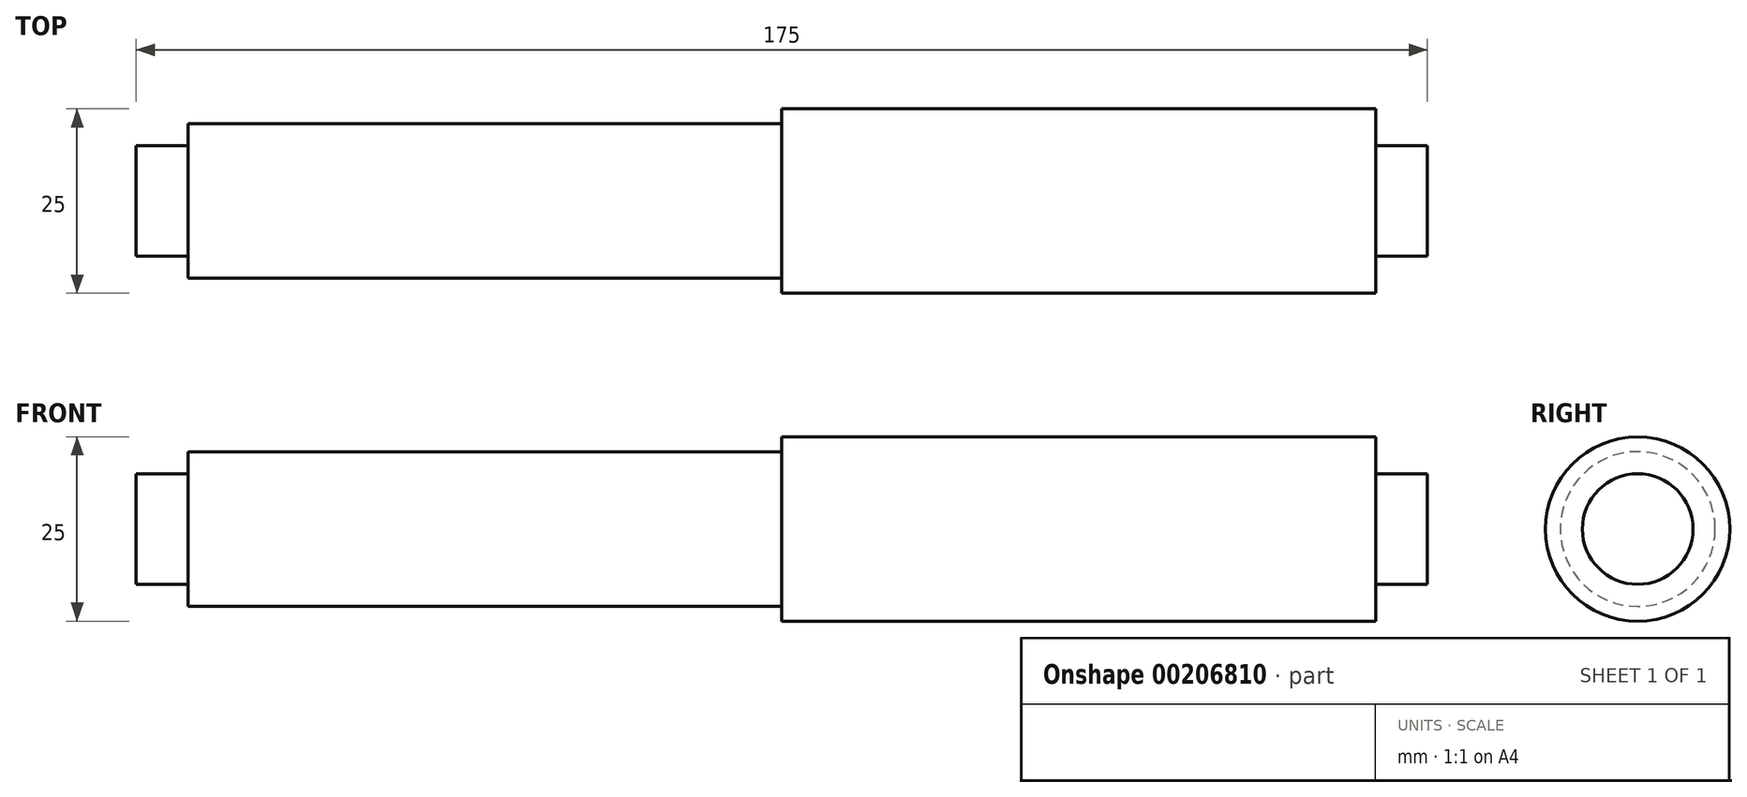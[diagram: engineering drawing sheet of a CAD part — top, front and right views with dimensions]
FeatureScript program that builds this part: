
annotation { "Feature Type Name" : "Feature", "Feature Type Description" : "" }
export const myFeature = defineFeature(function(context is Context, id is Id, definition is map)
    precondition{}
    {
        {
            var Q0;
            Q0=qCreatedBy(makeId("Front.planeOp"),FACE);
            var sketch = newSketch(context, id + "F0", { "sketchPlane" : qUnion([Q0])});
            skLineSegment(sketch, "E0.bottom", {"start": v(80.5, -12.5) * mm, "end": v(0, -12.5) * mm});
            skLineSegment(sketch, "E0.top", {"start": v(80.5, 12.5) * mm, "end": v(0, 12.5) * mm});
            skLineSegment(sketch, "E0.left", {"start": v(80.5, -12.5) * mm, "end": v(80.5, 7.5) * mm});
            skLineSegment(sketch, "E0.right", {"start": v(-80.5, -10.5) * mm, "end": v(-80.5, 0) * mm});
            skPoint(sketch, "E0.middle", {"position": v(0, 0) * mm});
            skLineSegment(sketch, "E1.bottom", {"start": v(0, -10.5) * mm, "end": v(-80.5, -10.5) * mm});
            skLineSegment(sketch, "E1.top", {"start": v(0, 10.5) * mm, "end": v(-80.5, 10.5) * mm});
            skLineSegment(sketch, "E1.right", {"start": v(-80.5, -10.5) * mm, "end": v(-80.5, -7.5) * mm});
            skLineSegment(sketch, "E2.bottom", {"start": v(87.5, -7.5) * mm, "end": v(80.5, -7.5) * mm});
            skLineSegment(sketch, "E2.top", {"start": v(87.5, 7.5) * mm, "end": v(80.5, 7.5) * mm});
            skLineSegment(sketch, "E2.left", {"start": v(87.5, -7.5) * mm, "end": v(87.5, 7.5) * mm});
            skLineSegment(sketch, "E2.right", {"start": v(-87.5, -7.5) * mm, "end": v(-87.5, 7.5) * mm});
            skLineSegment(sketch, "E3", {"start": v(0, 12.5) * mm, "end": v(0, -12.5) * mm});
            skLineSegment(sketch, "E4.trimOffspring", {"start": v(-80.5, -7.5) * mm, "end": v(-87.5, -7.5) * mm});
            skLineSegment(sketch, "E5.trimOffspring", {"start": v(-80.5, 7.5) * mm, "end": v(-87.5, 7.5) * mm});
            skLineSegment(sketch, "E6", {"start": v(-60.52, 0) * mm, "end": v(0, 0) * mm});
            skPoint(sketch, "E7.orphan", {"position": v(-80.5, 12.5) * mm});
            skPoint(sketch, "E8.orphan", {"position": v(-80.5, -12.5) * mm});
            skLineSegment(sketch, "E9", {"start": v(-87.5, 0) * mm, "end": v(87.5, 0) * mm});
            skLineSegment(sketch, "E10.trimOffspring", {"start": v(-80.5, 0) * mm, "end": v(-80.5, 10.5) * mm});
            skLineSegment(sketch, "E11.trimOffspring", {"start": v(-80.5, 7.5) * mm, "end": v(-80.5, 10.5) * mm});
            skLineSegment(sketch, "E12.trimOffspring", {"start": v(80.5, 7.5) * mm, "end": v(80.5, 10.5) * mm});
            skLineSegment(sketch, "E13.trimOffspring", {"start": v(80.5, 10.5) * mm, "end": v(80.5, 12.5) * mm});
            skPoint(sketch, "E1.left.start.orphan", {"position": v(80.5, -10.5) * mm});
            skSolve(sketch);
        }
        {
            var Q0;
            {var subQ0=sQuery(id+"F0.wireOp",EDGE,"E0.right");Q0=makeQuery(id+"F0.imprint","IMPRINT",FACE,{"disambiguationData":[TD([[makeQuery(id+"F0.imprint","IMPRINT",EDGE,{"derivedFrom":subQ0}),1.0]])]});}
            var Q1;
            {var subQ4=sQuery(id+"F0.wireOp",EDGE,"E0.right");Q1=makeQuery(id+"F0.imprint","IMPRINT",FACE,{"disambiguationData":[TD([[makeQuery(id+"F0.imprint","IMPRINT",EDGE,{"derivedFrom":subQ4}),-1.0]])]});}
            var Q2;
            {var subQ7=sQuery(id+"F0.wireOp",EDGE,"E0.bottom");Q2=makeQuery(id+"F0.imprint","IMPRINT",FACE,{"disambiguationData":[TD([[makeQuery(id+"F0.imprint","IMPRINT",EDGE,{"derivedFrom":subQ7}),-1.0]])]});}
            var Q3;
            {var subQ0=sQuery(id+"F0.wireOp",EDGE,"E2.bottom");Q3=makeQuery(id+"F0.imprint","IMPRINT",FACE,{"disambiguationData":[TD([[makeQuery(id+"F0.imprint","IMPRINT",EDGE,{"derivedFrom":subQ0}),-1.0]])]});}
            var Q4;
            Q4=sQuery(id+"F0.wireOp",EDGE,"E9");
            revolve(context, id + "F1", {"entities" : qUnion([Q0, Q1, Q2, Q3]), "axis" : qUnion([Q4]), "revolveType" : RevolveType.FULL});
        }
    });
